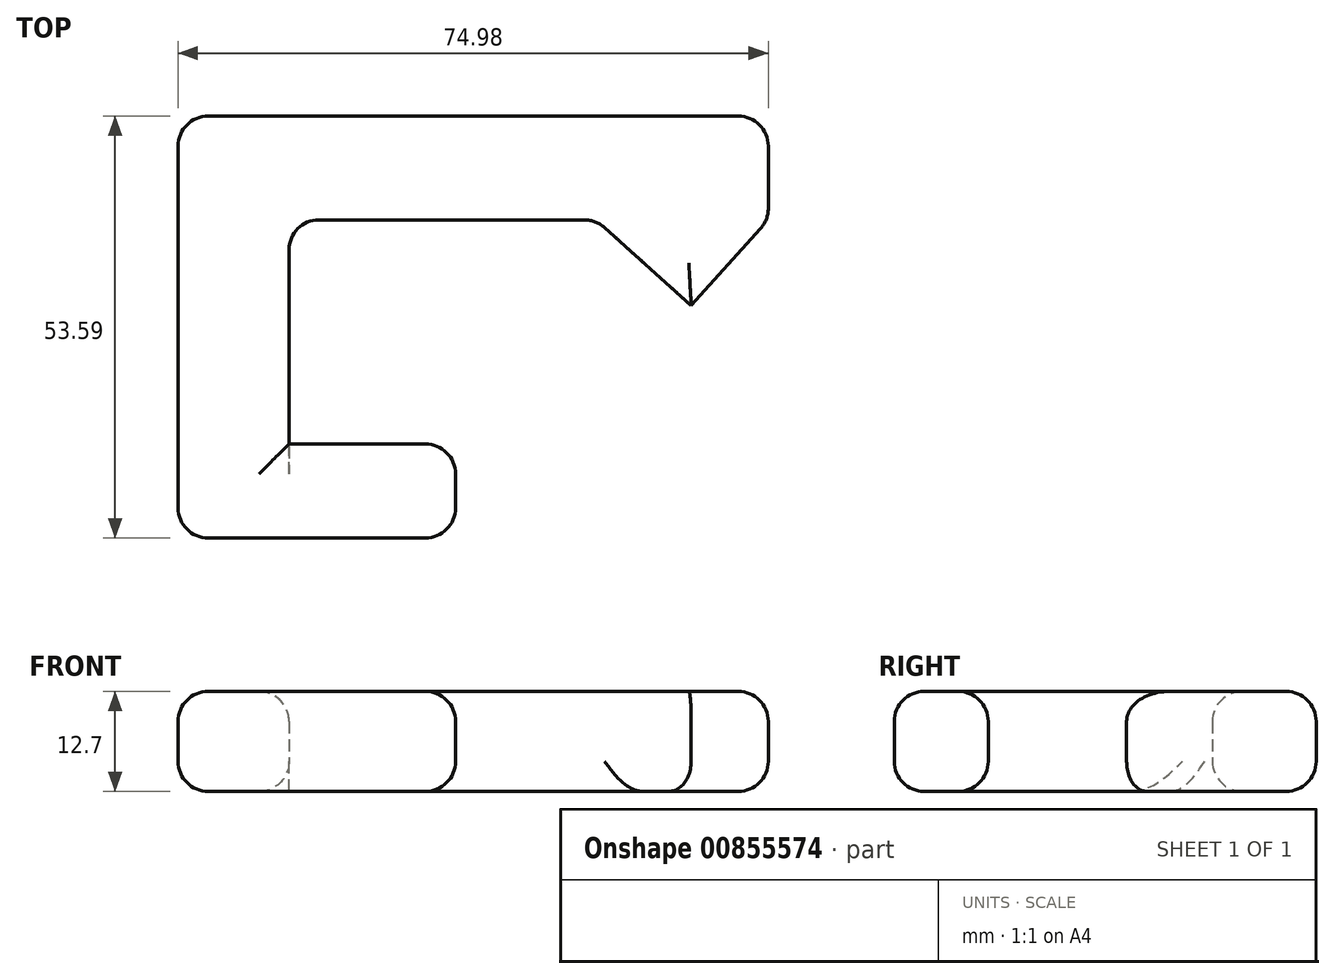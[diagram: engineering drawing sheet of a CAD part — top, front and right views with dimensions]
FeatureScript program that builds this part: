
annotation { "Feature Type Name" : "Feature", "Feature Type Description" : "" }
export const myFeature = defineFeature(function(context is Context, id is Id, definition is map)
    precondition{}
    {
        {
            var Q0;
            Q0=qCreatedBy(makeId("Top.planeOp"),FACE);
            var sketch = newSketch(context, id + "F0", { "sketchPlane" : qUnion([Q0])});
            skLineSegment(sketch, "E0", {"start": v(-35.24, 0) * mm, "end": v(-35.24, 53.59) * mm});
            skLineSegment(sketch, "E1", {"start": v(-35.24, 53.59) * mm, "end": v(39.74, 53.59) * mm});
            skLineSegment(sketch, "E2", {"start": v(39.74, 53.59) * mm, "end": v(39.74, 40.4) * mm});
            skLineSegment(sketch, "E3", {"start": v(17.85, 40.4) * mm, "end": v(-21.14, 40.4) * mm});
            skLineSegment(sketch, "E4", {"start": v(-21.14, 40.4) * mm, "end": v(-21.14, 11.93) * mm});
            skLineSegment(sketch, "E5", {"start": v(-21.14, 11.93) * mm, "end": v(0, 11.93) * mm});
            skLineSegment(sketch, "E6", {"start": v(0, 11.93) * mm, "end": v(0, 0) * mm});
            skLineSegment(sketch, "E7", {"start": v(0, 0) * mm, "end": v(-35.24, 0) * mm});
            skLineSegment(sketch, "E8", {"start": v(39.74, 40.4) * mm, "end": v(29.94, 29.52) * mm});
            skLineSegment(sketch, "E9", {"start": v(29.94, 29.52) * mm, "end": v(17.85, 40.4) * mm});
            skSolve(sketch);
        }
        {
            var Q0;
            Q0=makeQuery(id+"F0.imprint","IMPRINT",FACE,{"disambiguationData":[TD([[makeQuery(id+"F0.imprint","IMPRINT",EDGE,{"derivedFrom":sQuery(id+"F0.wireOp",EDGE,"E0")}),-1.0]])]});
            extrude(context, id + "F1", {"entities" : qUnion([Q0]), "depth" : 12.7 * mm, "offsetDistance" : 25.4 * mm});
        }
        {
            var Q0;
            Q0=makeQuery(id+"F1.opExtrude","CAP_EDGE",EDGE,{"disambiguationData":[OSD([sQuery(id+"F0.wireOp",EDGE,"E7")])],"isStart":false});
            var Q1;
            Q1=makeQuery(id+"F1.opExtrude","CAP_EDGE",EDGE,{"disambiguationData":[OSD([sQuery(id+"F0.wireOp",EDGE,"E0")])],"isStart":false});
            fillet(context, id + "F2", {"entities" : qUnion([Q0, Q1]), "radius" : 3.8 * mm, "tangentPropagation" : true, "allowEdgeOverflow" : false});
        }
        {
            var Q0;
            Q0=makeQuery(id+"F1.opExtrude","CAP_EDGE",EDGE,{"disambiguationData":[OSD([sQuery(id+"F0.wireOp",EDGE,"E1")])],"isStart":false});
            var Q1;
            Q1=makeQuery(id+"F1.opExtrude","CAP_EDGE",EDGE,{"disambiguationData":[OSD([sQuery(id+"F0.wireOp",EDGE,"E5")])],"isStart":false});
            var Q2;
            Q2=makeQuery(id+"F1.opExtrude","CAP_EDGE",EDGE,{"disambiguationData":[OSD([sQuery(id+"F0.wireOp",EDGE,"E3")])],"isStart":false});
            var Q3;
            Q3=makeQuery(id+"F1.opExtrude","SWEPT_FACE",FACE,{"disambiguationData":[OSD([sQuery(id+"F0.wireOp",EDGE,"E3")])]});
            var Q4;
            Q4=makeQuery(id+"F1.opExtrude","SWEPT_EDGE",EDGE,{"disambiguationData":[OSD([sQuery(id+"F0.wireOp",EDGE,"E3"),sQuery(id+"F0.wireOp",EDGE,"E4")])]});
            var Q5;
            Q5=makeQuery(id+"F1.opExtrude","CAP_FACE",FACE,{"disambiguationData":[OSD([sQuery(id+"F0.wireOp",EDGE,"E0"),sQuery(id+"F0.wireOp",EDGE,"E1"),sQuery(id+"F0.wireOp",EDGE,"E2"),sQuery(id+"F0.wireOp",EDGE,"E3"),sQuery(id+"F0.wireOp",EDGE,"E4"),sQuery(id+"F0.wireOp",EDGE,"E5"),sQuery(id+"F0.wireOp",EDGE,"E6"),sQuery(id+"F0.wireOp",EDGE,"E7"),sQuery(id+"F0.wireOp",EDGE,"E8"),sQuery(id+"F0.wireOp",EDGE,"E9")])],"isStart":false});
            var Q6;
            Q6=makeQuery(id+"F1.opExtrude","CAP_EDGE",EDGE,{"disambiguationData":[OSD([sQuery(id+"F0.wireOp",EDGE,"E9")])],"isStart":false});
            fillet(context, id + "F3", {"entities" : qUnion([Q0, Q1, Q2, Q3, Q4, Q5, Q6]), "radius" : 3.8 * mm, "tangentPropagation" : true, "allowEdgeOverflow" : false});
        }
        {
            var Q0;
            Q0=makeQuery(id+"F1.opExtrude","CAP_EDGE",EDGE,{"disambiguationData":[OSD([sQuery(id+"F0.wireOp",EDGE,"E5")])],"isStart":true});
            var Q1;
            Q1=makeQuery(id+"F1.opExtrude","CAP_EDGE",EDGE,{"disambiguationData":[OSD([sQuery(id+"F0.wireOp",EDGE,"E6")])],"isStart":true});
            var Q2;
            Q2=makeQuery(id+"F3.opFillet","BLEND_EDGE",EDGE,{"blendedFrom":[makeQuery(id+"F1.opExtrude","CAP_EDGE",EDGE,{"disambiguationData":[OSD([sQuery(id+"F0.wireOp",EDGE,"E9")])],"isStart":true}),makeQuery(id+"F1.opExtrude","SWEPT_FACE",FACE,{"disambiguationData":[OSD([sQuery(id+"F0.wireOp",EDGE,"E8")])]})],"blendedInto":[makeQuery(id+"F1.opExtrude","SWEPT_FACE",FACE,{"disambiguationData":[OSD([sQuery(id+"F0.wireOp",EDGE,"E8")])]})]});
            var Q3;
            Q3=makeQuery(id+"F1.opExtrude","CAP_EDGE",EDGE,{"disambiguationData":[OSD([sQuery(id+"F0.wireOp",EDGE,"E8")])],"isStart":true});
            var Q4;
            Q4=makeQuery(id+"F1.opExtrude","CAP_EDGE",EDGE,{"disambiguationData":[OSD([sQuery(id+"F0.wireOp",EDGE,"E2")])],"isStart":true});
            var Q5;
            Q5=makeQuery(id+"F1.opExtrude","CAP_EDGE",EDGE,{"disambiguationData":[OSD([sQuery(id+"F0.wireOp",EDGE,"E1")])],"isStart":true});
            fillet(context, id + "F4", {"entities" : qUnion([Q0, Q1, Q2, Q3, Q4, Q5]), "radius" : 3.8 * mm, "tangentPropagation" : true, "allowEdgeOverflow" : false});
        }
        {
            var Q0;
            Q0=makeQuery(id+"F1.opExtrude","SWEPT_EDGE",EDGE,{"disambiguationData":[OSD([sQuery(id+"F0.wireOp",EDGE,"E0"),sQuery(id+"F0.wireOp",EDGE,"E7")])]});
            var Q1;
            Q1=makeQuery(id+"F1.opExtrude","SWEPT_EDGE",EDGE,{"disambiguationData":[OSD([sQuery(id+"F0.wireOp",EDGE,"E1"),sQuery(id+"F0.wireOp",EDGE,"E2")])]});
            var Q2;
            Q2=makeQuery(id+"F1.opExtrude","SWEPT_EDGE",EDGE,{"disambiguationData":[OSD([sQuery(id+"F0.wireOp",EDGE,"E5"),sQuery(id+"F0.wireOp",EDGE,"E6")])]});
            var Q3;
            Q3=makeQuery(id+"F1.opExtrude","SWEPT_EDGE",EDGE,{"disambiguationData":[OSD([sQuery(id+"F0.wireOp",EDGE,"E2"),sQuery(id+"F0.wireOp",EDGE,"E8")])]});
            fillet(context, id + "F5", {"entities" : qUnion([Q0, Q1, Q2, Q3]), "radius" : 3.8 * mm, "tangentPropagation" : true, "allowEdgeOverflow" : false});
        }
    });
